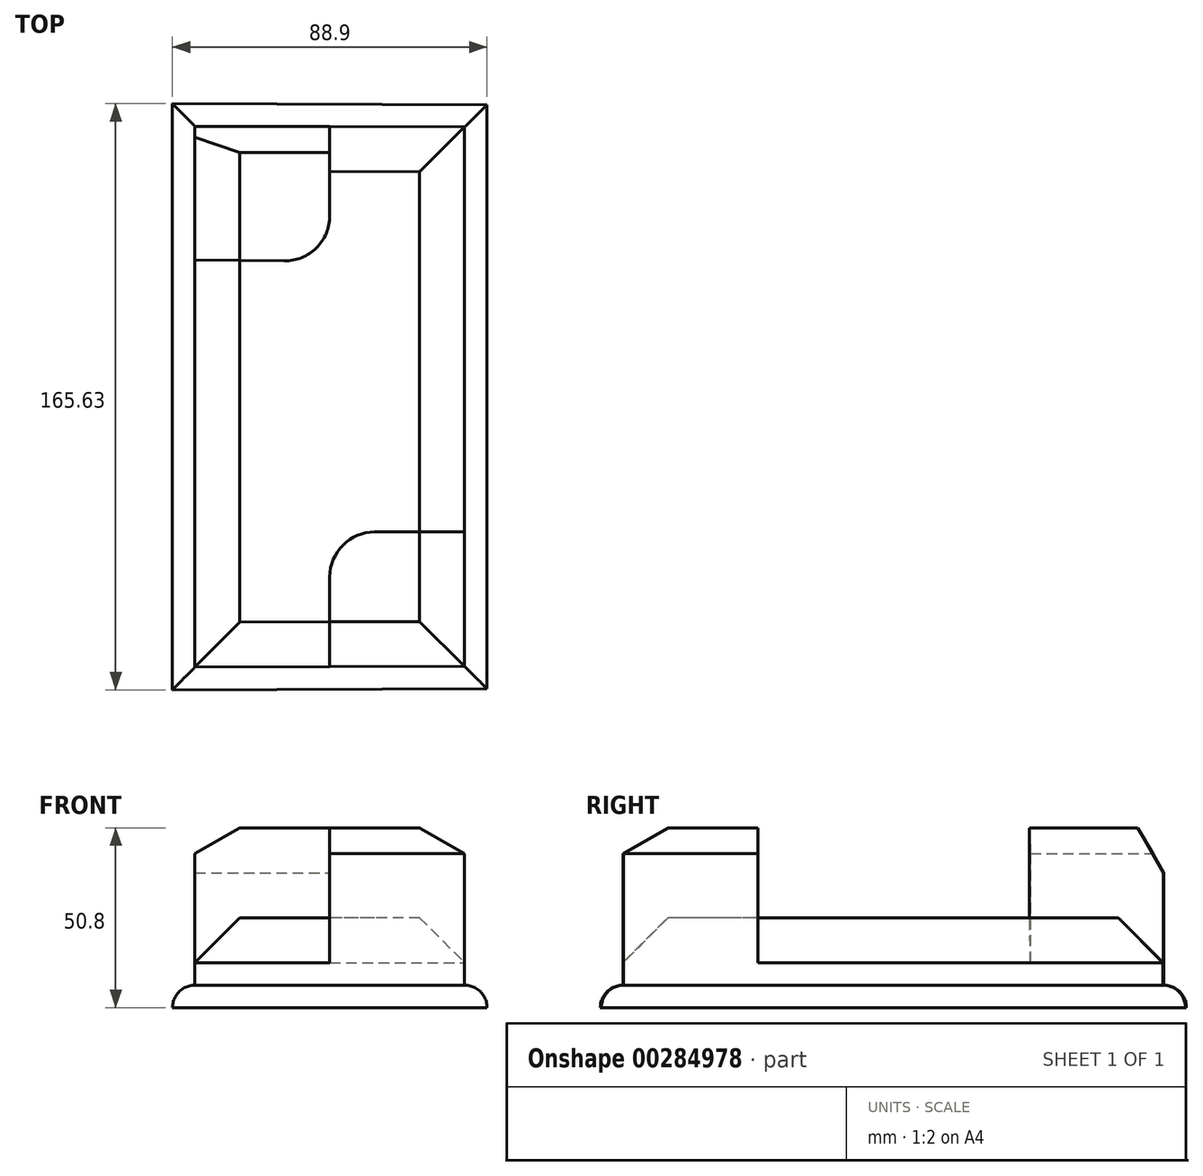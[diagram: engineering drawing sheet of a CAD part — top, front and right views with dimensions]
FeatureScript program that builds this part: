
annotation { "Feature Type Name" : "Feature", "Feature Type Description" : "" }
export const myFeature = defineFeature(function(context is Context, id is Id, definition is map)
    precondition{}
    {
        {
            var Q0;
            Q0=qCreatedBy(makeId("Top.planeOp"),FACE);
            var sketch = newSketch(context, id + "F0", { "sketchPlane" : qUnion([Q0])});
            skLineSegment(sketch, "E0", {"start": v(-115.35, 62.36) * mm, "end": v(-115.35, -90.53) * mm});
            skLineSegment(sketch, "E1", {"start": v(-39.15, 62.11) * mm, "end": v(-39.15, -90.29) * mm});
            skLineSegment(sketch, "E2", {"start": v(-115.35, 62.36) * mm, "end": v(-39.15, 62.11) * mm});
            skLineSegment(sketch, "E3", {"start": v(-115.35, -90.53) * mm, "end": v(-39.15, -90.29) * mm});
            skLineSegment(sketch, "E4.0", {"start": v(-121.7, 68.73) * mm, "end": v(-32.8, 68.44) * mm});
            skLineSegment(sketch, "E4.1", {"start": v(-121.7, 68.73) * mm, "end": v(-121.7, -96.9) * mm});
            skLineSegment(sketch, "E4.2", {"start": v(-121.7, -96.9) * mm, "end": v(-32.8, -96.62) * mm});
            skLineSegment(sketch, "E4.3", {"start": v(-32.8, 68.44) * mm, "end": v(-32.8, -96.62) * mm});
            skArc(sketch, "E5", {"start": v(-90.11, 24.3) * mm, "mid": v(-81.02, 27.96) * mm, "end": v(-77.25, 37) * mm});
            skArc(sketch, "E6", {"start": v(-64.55, -52.3) * mm, "mid": v(-73.53, -56.03) * mm, "end": v(-77.25, -65) * mm});
            skLineSegment(sketch, "E7", {"start": v(-77.25, 37) * mm, "end": v(-77.25, 62.24) * mm});
            skLineSegment(sketch, "E8", {"start": v(-90.11, 24.3) * mm, "end": v(-115.35, 24.62) * mm});
            skLineSegment(sketch, "E9", {"start": v(-77.25, -65) * mm, "end": v(-77.25, -90.4) * mm});
            skLineSegment(sketch, "E10", {"start": v(-39.15, -52.3) * mm, "end": v(-64.55, -52.3) * mm});
            skSolve(sketch);
        }
        {
            var Q0;
            Q0=makeQuery(id+"F0.imprint","IMPRINT",FACE,{"disambiguationData":[TD([[makeQuery(id+"F0.imprint","IMPRINT",EDGE,{"derivedFrom":sQuery(id+"F0.wireOp",EDGE,"E4.0")}),-1.0]])]});
            extrude(context, id + "F1", {"entities" : qUnion([Q0]), "depth" : 6.35 * mm});
        }
        {
            var Q0;
            Q0=makeQuery(id+"F0.imprint","IMPRINT",FACE,{"disambiguationData":[TD([[makeQuery(id+"F0.imprint","IMPRINT",EDGE,{"derivedFrom":sQuery(id+"F0.wireOp",EDGE,"E5")}),-1.0]])]});
            extrude(context, id + "F2", {"entities" : qUnion([Q0]), "operationType" : NewBodyOperationType.ADD, "depth" : 25.4 * mm});
        }
        {
            var Q0;
            Q0=makeQuery(id+"F0.imprint","IMPRINT",FACE,{"disambiguationData":[TD([[makeQuery(id+"F0.imprint","IMPRINT",EDGE,{"derivedFrom":sQuery(id+"F0.wireOp",EDGE,"E6")}),1.0]])]});
            var Q1;
            Q1=makeQuery(id+"F0.imprint","IMPRINT",FACE,{"disambiguationData":[TD([[makeQuery(id+"F0.imprint","IMPRINT",EDGE,{"derivedFrom":sQuery(id+"F0.wireOp",EDGE,"E5")}),1.0]])]});
            extrude(context, id + "F3", {"entities" : qUnion([Q0, Q1]), "operationType" : NewBodyOperationType.ADD, "depth" : 50.8 * mm});
        }
        {
            var Q0;
            Q0=makeQuery(id+"F1.opExtrude","CAP_EDGE",EDGE,{"disambiguationData":[OSD([sQuery(id+"F0.wireOp",EDGE,"E4.2")])],"isStart":false});
            var Q1;
            Q1=makeQuery(id+"F1.opExtrude","CAP_EDGE",EDGE,{"disambiguationData":[OSD([sQuery(id+"F0.wireOp",EDGE,"E4.3")])],"isStart":false});
            var Q2;
            Q2=makeQuery(id+"F1.opExtrude","CAP_EDGE",EDGE,{"disambiguationData":[OSD([sQuery(id+"F0.wireOp",EDGE,"E4.0")])],"isStart":false});
            var Q3;
            Q3=makeQuery(id+"F1.opExtrude","CAP_EDGE",EDGE,{"disambiguationData":[OSD([sQuery(id+"F0.wireOp",EDGE,"E4.1")])],"isStart":false});
            fillet(context, id + "F4", {"entities" : qUnion([Q0, Q1, Q2, Q3]), "radius" : 6.35 * mm, "tangentPropagation" : true, "allowEdgeOverflow" : false});
        }
        {
            var Q0;
            Q0=makeQuery(id+"F2.opExtrude","CAP_EDGE",EDGE,{"disambiguationData":[OSD([sQuery(id+"F0.wireOp",EDGE,"E3")])],"isStart":false});
            var Q1;
            Q1=makeQuery(id+"F2.opExtrude","CAP_EDGE",EDGE,{"disambiguationData":[OSD([sQuery(id+"F0.wireOp",EDGE,"E1")])],"isStart":false});
            var Q2;
            Q2=makeQuery(id+"F2.opExtrude","CAP_EDGE",EDGE,{"disambiguationData":[OSD([sQuery(id+"F0.wireOp",EDGE,"E0")])],"isStart":false});
            var Q3;
            Q3=makeQuery(id+"F2.opExtrude","CAP_EDGE",EDGE,{"disambiguationData":[OSD([sQuery(id+"F0.wireOp",EDGE,"E2")])],"isStart":false});
            chamfer(context, id + "F5", {"entities" : qUnion([Q0, Q1, Q2, Q3]), "width" : 12.7 * mm, "tangentPropagation" : true});
        }
        {
            var Q0;
            Q0=makeQuery(id+"F3.opExtrude","CAP_EDGE",EDGE,{"disambiguationData":[OSD([sQuery(id+"F0.wireOp",EDGE,"E3")])],"isStart":false});
            var Q1;
            Q1=makeQuery(id+"F3.opExtrude","CAP_EDGE",EDGE,{"disambiguationData":[OSD([sQuery(id+"F0.wireOp",EDGE,"E1")])],"isStart":false});
            var Q2;
            Q2=makeQuery(id+"F3.opExtrude","CAP_EDGE",EDGE,{"disambiguationData":[OSD([sQuery(id+"F0.wireOp",EDGE,"E0")])],"isStart":false});
            var Q3;
            Q3=makeQuery(id+"F3.opExtrude","CAP_EDGE",EDGE,{"disambiguationData":[OSD([sQuery(id+"F0.wireOp",EDGE,"E2")])],"isStart":false});
            chamfer(context, id + "F6", {"entities" : qUnion([Q0, Q1, Q2, Q3]), "chamferType" : ChamferType.OFFSET_ANGLE, "width" : 12.7 * mm, "oppositeDirection" : false, "angle" : 30 * degree, "tangentPropagation" : true});
        }
    });
